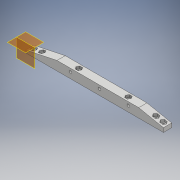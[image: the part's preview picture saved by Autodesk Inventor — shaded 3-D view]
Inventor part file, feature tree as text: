
AUTODESK INVENTOR PART (.ipt)
format: ipt  version: 2017 (Build 210142000, 142)  size: 217,088 bytes
history: native  units: mm
features: sketch x9, extrude x9, plane x7
ambient origin geometry x8: Origin, YZ Plane, XZ Plane, XY Plane, X Axis, Y Axis, Z Axis, Center Point
bodies: Solid1 (feature_tree)
feature tree (25):
  sketch  "Sketch1"  dims[d1=10.0mm d2=90.0deg]
  plane  "Work Plane2"
  sketch  "Sketch2"  dims[d4=3.2mm d6=3.2mm]
  plane  "Work Plane1"
  extrude  "klocek"  TaperAngle=90.0deg  [1 undecoded]
  plane  "Work Plane3"
  extrude  "prowadzenie osi"  Depth=3.2mm
  plane  "Work Plane4"
  sketch  "Sketch7"  dims[d9=42.5mm d13=3.2mm]
  sketch  "Sketch8"  dims[d15=3.2mm d16=70.0mm]
  extrude  "przedni skos"  Depth=60.0mm
  extrude  "tylni skos"  Depth=3.2mm
  plane  "Work Plane7"
  sketch  "Sketch5"  dims[d7=3.2mm d8=60.0mm]
  extrude  "hex insert middle"  Depth=70.0mm
  plane  "Work Plane6"
  sketch  "Sketch9"  dims[d17=3.2mm d18=35.0mm]
  extrude  "hex insert rear 1"  Depth=35.0mm
  plane  "Work Plane5"
  extrude  "hex insert rear 2"  Depth=3.2mm
  extrude  "Extrusion18"  Depth=5.0mm
  extrude  "Extrusion19"  Depth=5.9mm
  sketch  "Sketch10"  dims[d26=3.2mm d27=33.5mm d28=3.2mm d29=44.5mm]
  sketch  "Sketch13"  dims[d32=15.0mm d33=5.0mm]
  sketch  "Sketch16"  dims[d38=11.0mm d39=0.0mm d44=5.9mm d45=5.9mm d51=5.9mm d61=3.2mm d62=10.0mm d63=9.0mm d64=54.5mm d65=35.0mm d67=11.0mm d68=0.0mm d70=6.0mm d71=0.0mm d72=5.9mm d77=5.0mm d78=0.0mm d80=6.0mm d81=30.0mm d82=3.0mm d83=0.0mm d84=7.5mm d85=0.0mm d86=8.0mm d87=38.0mm d88=7.0mm d89=0.0mm d90=5.9mm d91=9.0mm d92=0.0mm d93=5.9mm d94=7.5mm d95=0.0mm]
note: 1 required parameter value undecoded (feature->parameter linkage not recoverable at this tier; creation-order binding heuristic only, values carry confidence <= 0.55)
